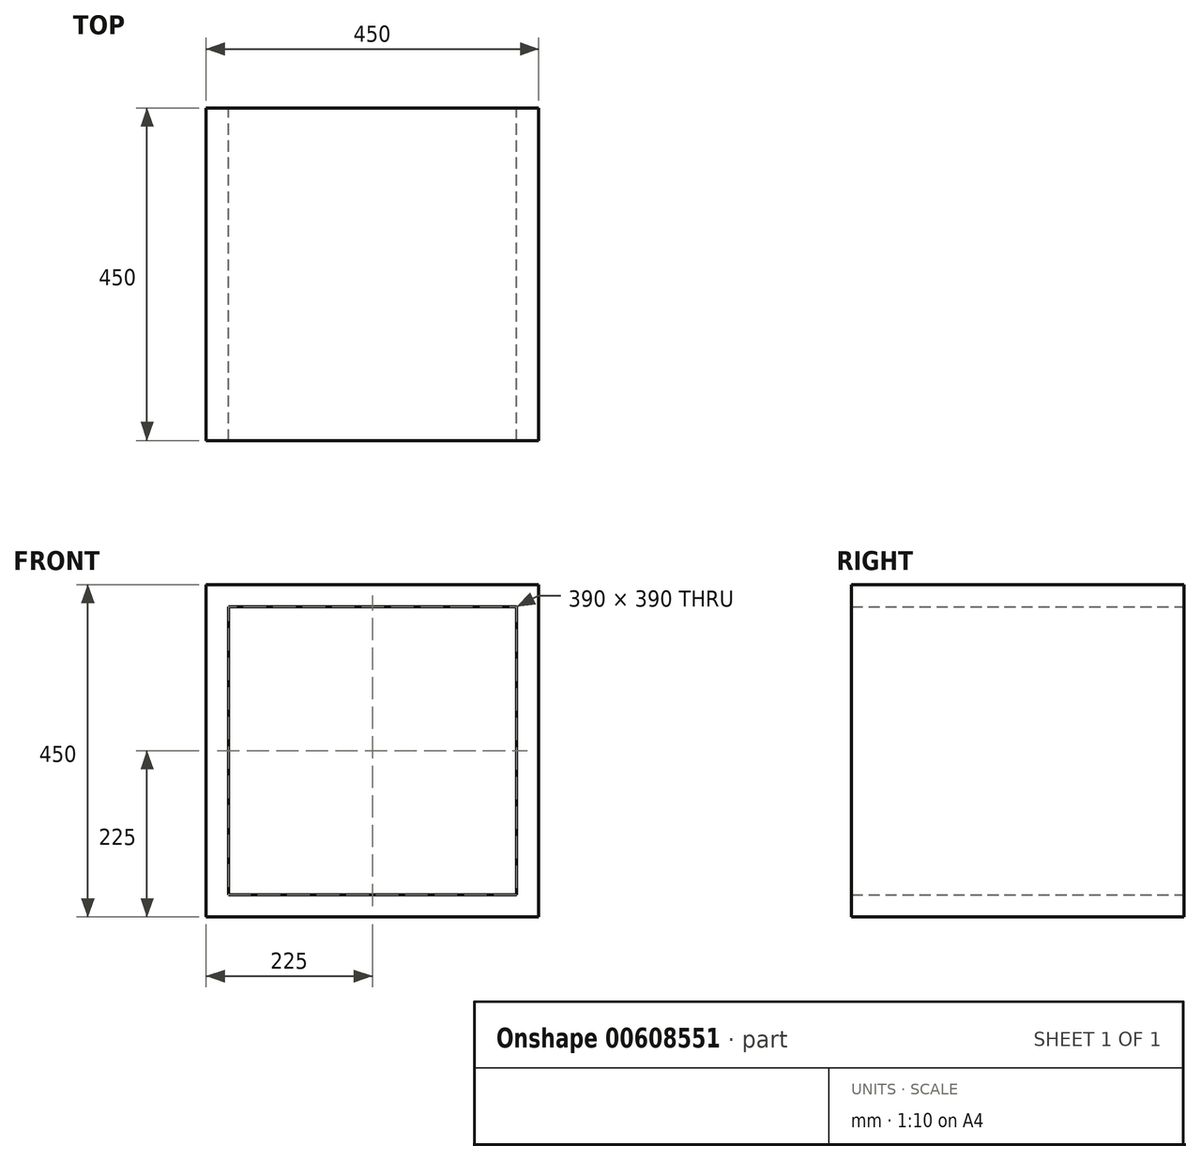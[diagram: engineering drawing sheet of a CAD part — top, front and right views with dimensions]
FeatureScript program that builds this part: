
annotation { "Feature Type Name" : "Feature", "Feature Type Description" : "" }
export const myFeature = defineFeature(function(context is Context, id is Id, definition is map)
    precondition{}
    {
        {
            assignVariable(context, id + "F0", {"name" : "depth", "anyValue" : 450});
        }
        {
            var Q0;
            Q0=qCreatedBy(makeId("Front.planeOp"),FACE);
            var sketch = newSketch(context, id + "F1", { "sketchPlane" : qUnion([Q0])});
            skLineSegment(sketch, "E0.bottom", {"start": v(225, 225) * mm, "end": v(-225, 225) * mm});
            skLineSegment(sketch, "E0.top", {"start": v(225, -225) * mm, "end": v(-225, -225) * mm});
            skLineSegment(sketch, "E0.left", {"start": v(225, 225) * mm, "end": v(225, -225) * mm});
            skLineSegment(sketch, "E0.right", {"start": v(-225, 225) * mm, "end": v(-225, -225) * mm});
            skPoint(sketch, "E0.middle", {"position": v(0, 0) * mm});
            skLineSegment(sketch, "E1.0", {"start": v(195, 195) * mm, "end": v(195, -195) * mm});
            skLineSegment(sketch, "E1.1", {"start": v(195, 195) * mm, "end": v(-195, 195) * mm});
            skLineSegment(sketch, "E1.2", {"start": v(-195, 195) * mm, "end": v(-195, -195) * mm});
            skLineSegment(sketch, "E1.3", {"start": v(195, -195) * mm, "end": v(-195, -195) * mm});
            skSolve(sketch);
        }
        {
            var Q0;
            Q0=makeQuery(id+"F1.imprint","IMPRINT",FACE,{"disambiguationData":[TD([[makeQuery(id+"F1.imprint","IMPRINT",EDGE,{"derivedFrom":sQuery(id+"F1.wireOp",EDGE,"E0.bottom")}),1.0]])]});
            extrude(context, id + "F2", {"entities" : qUnion([Q0]), "depth" : getVariable(context, 'depth') * mm, "offsetDistance" : 25 * mm});
        }
    });
